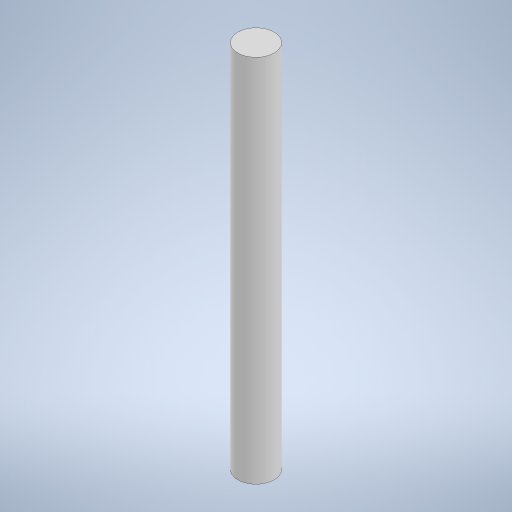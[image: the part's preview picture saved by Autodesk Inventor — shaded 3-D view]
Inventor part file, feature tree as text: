
AUTODESK INVENTOR PART (.ipt)
format: ipt  version: 2024 (Build 280153000, 153)  size: 230,912 bytes
history: native  units: in
note: dims shown in document units (in); Inventor stores cm internally (conversion verified against a paired STEP export)
features: extrude x1, sketch x1
ambient origin geometry x8: Origin, YZ Plane, XZ Plane, XY Plane, X Axis, Y Axis, Z Axis, Center Point
bodies: Body1 (feature_tree)
feature tree (2):
  extrude  "Extrusion4"  Depth=10.0in TaperAngle=0.0deg
  sketch  "Sketch4"  dims[d22=0.9843in d23=10.0in d24=0.0in]
